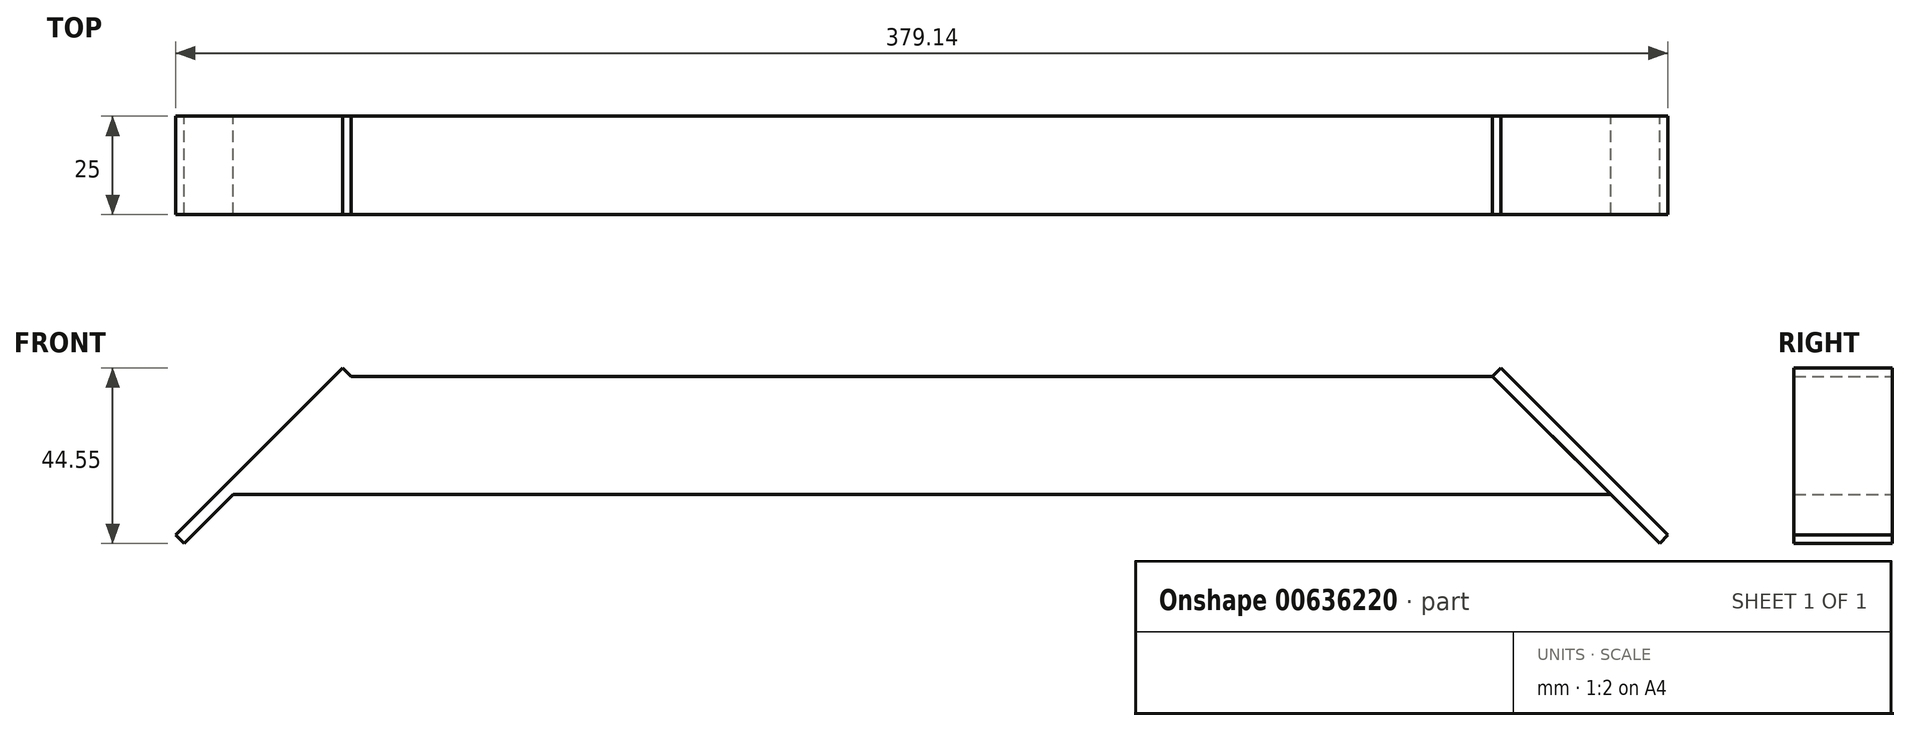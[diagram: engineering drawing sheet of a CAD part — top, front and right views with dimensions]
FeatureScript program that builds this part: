
annotation { "Feature Type Name" : "Feature", "Feature Type Description" : "" }
export const myFeature = defineFeature(function(context is Context, id is Id, definition is map)
    precondition{}
    {
        {
            var Q0;
            Q0=qCreatedBy(makeId("Front.planeOp"),FACE);
            var sketch = newSketch(context, id + "F0", { "sketchPlane" : qUnion([Q0])});
            skLineSegment(sketch, "E0", {"start": v(0, 0) * mm, "end": v(350, 0) * mm});
            skLineSegment(sketch, "E1", {"start": v(350, 0) * mm, "end": v(350, -30) * mm});
            skLineSegment(sketch, "E2", {"start": v(350, -30) * mm, "end": v(0, -30) * mm});
            skLineSegment(sketch, "E3", {"start": v(0, -30) * mm, "end": v(0, 0) * mm});
            skLineSegment(sketch, "E4", {"start": v(0, -30) * mm, "end": v(30, 0) * mm});
            skLineSegment(sketch, "E5", {"start": v(350, -30) * mm, "end": v(320, 0) * mm});
            skLineSegment(sketch, "E6", {"start": v(30, 0) * mm, "end": v(-12.43, -42.43) * mm});
            skLineSegment(sketch, "E7", {"start": v(-12.43, -42.43) * mm, "end": v(-14.55, -40.3) * mm});
            skLineSegment(sketch, "E8", {"start": v(-14.55, -40.3) * mm, "end": v(27.88, 2.12) * mm});
            skLineSegment(sketch, "E9", {"start": v(27.88, 2.12) * mm, "end": v(30, 0) * mm});
            skLineSegment(sketch, "E10", {"start": v(320, 0) * mm, "end": v(362.47, -42.38) * mm});
            skLineSegment(sketch, "E11", {"start": v(362.47, -42.38) * mm, "end": v(364.59, -40.26) * mm});
            skLineSegment(sketch, "E12", {"start": v(364.59, -40.26) * mm, "end": v(335, -10.73) * mm});
            skPoint(sketch, "E12.endSnap0", {"position": v(335, -15) * mm});
            skLineSegment(sketch, "E13", {"start": v(320, 0) * mm, "end": v(322.12, 2.12) * mm});
            skLineSegment(sketch, "E14", {"start": v(322.12, 2.12) * mm, "end": v(335, -10.73) * mm});
            skSolve(sketch);
        }
        {
            var Q0;
            {var subQ4=sQuery(id+"F0.wireOp",EDGE,"E2");Q0=makeQuery(id+"F0.imprint","IMPRINT",FACE,{"disambiguationData":[TD([[makeQuery(id+"F0.imprint","IMPRINT",EDGE,{"derivedFrom":subQ4}),-1.0]])]});}
            var Q1;
            {var subQ1=sQuery(id+"F0.wireOp",EDGE,"E0");var subQ3=sQuery(id+"F0.wireOp",EDGE,"E8");var subQ4=makeQuery(id+"F0.imprint","INTERSECT",VERTEX,{"derivedFrom":[subQ1,subQ3]});Q1=makeQuery(id+"F0.imprint","IMPRINT",FACE,{"disambiguationData":[TD([[makeQuery(id+"F0.imprint","IMPRINT",EDGE,{"disambiguationData":[TD([[subQ4,1.0]])],"derivedFrom":subQ3}),-1.0]])]});}
            var Q2;
            {var subQ5=sQuery(id+"F0.wireOp",EDGE,"E7");Q2=makeQuery(id+"F0.imprint","IMPRINT",FACE,{"disambiguationData":[TD([[makeQuery(id+"F0.imprint","IMPRINT",EDGE,{"derivedFrom":subQ5}),-1.0]])]});}
            var Q3;
            {var subQ0=sQuery(id+"F0.wireOp",EDGE,"E9");Q3=makeQuery(id+"F0.imprint","IMPRINT",FACE,{"disambiguationData":[TD([[makeQuery(id+"F0.imprint","IMPRINT",EDGE,{"derivedFrom":subQ0}),-1.0]])]});}
            var Q4;
            {var subQ3=sQuery(id+"F0.wireOp",EDGE,"E1");var subQ5=sQuery(id+"F0.wireOp",EDGE,"E12");var subQ6=makeQuery(id+"F0.imprint","INTERSECT",VERTEX,{"derivedFrom":[subQ3,subQ5]});Q4=makeQuery(id+"F0.imprint","IMPRINT",FACE,{"disambiguationData":[TD([[makeQuery(id+"F0.imprint","IMPRINT",EDGE,{"disambiguationData":[TD([[subQ6,-1.0]])],"derivedFrom":subQ3}),-1.0]])]});}
            var Q5;
            {var subQ0=sQuery(id+"F0.wireOp",EDGE,"E13");Q5=makeQuery(id+"F0.imprint","IMPRINT",FACE,{"disambiguationData":[TD([[makeQuery(id+"F0.imprint","IMPRINT",EDGE,{"derivedFrom":subQ0}),-1.0]])]});}
            var Q6;
            {var subQ5=sQuery(id+"F0.wireOp",EDGE,"E11");Q6=makeQuery(id+"F0.imprint","IMPRINT",FACE,{"disambiguationData":[TD([[makeQuery(id+"F0.imprint","IMPRINT",EDGE,{"derivedFrom":subQ5}),1.0]])]});}
            extrude(context, id + "F1", {"entities" : qUnion([Q0, Q1, Q2, Q3, Q4, Q5, Q6]), "depth" : 25 * mm, "offsetDistance" : 25 * mm});
        }
    });
